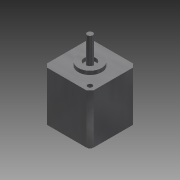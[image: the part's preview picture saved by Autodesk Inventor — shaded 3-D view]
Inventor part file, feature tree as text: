
AUTODESK INVENTOR PART (.ipt)
format: ipt  version: 2013 (Build 170138000, 138)  size: 138,240 bytes
history: native  units: in
note: dims shown in document units (in); Inventor stores cm internally (conversion verified against a paired STEP export)
features: extrude x5, sketch x5
ambient origin geometry x8: Origin, YZ Plane, XZ Plane, XY Plane, X Axis, Y Axis, Z Axis, Center Point
bodies: Solid1 (feature_tree)
feature tree (10):
  extrude  "Extrusion1"  Depth=1.0in
  extrude  "Extrusion2"  Depth=0.5in
  extrude  "Extrusion3"  Depth=0.0787in
  extrude  "Extrusion4"  Depth=0.0787in
  extrude  "Extrusion5"  Depth=0.0787in
  sketch  "Sketch1"  dims[d0=1.0in d2=1.0in]
  sketch  "Sketch2"  dims[d3=0.5in d4=0.5in]
  sketch  "Sketch3"  dims[d5=0.0787in d6=0.0787in]
  sketch  "Sketch4"  dims[d7=0.0787in d8=0.0787in]
  sketch  "Sketch5"  dims[d9=0.0787in d10=0.0787in d11=0.0787in d12=0.0787in d13=0.125in d14=0.125in d15=0.125in d16=0.125in d17=0.1in d18=0.1in d19=1.0625in d20=0.0in d21=0.5in d23=0.25in d24=0.0787in d25=0.0in d26=0.1181in d28=0.5906in d29=0.0in d30=0.1181in d32=0.4375in d33=0.0in d34=0.375in d35=0.375in d36=0.0625in d37=0.0625in d38=0.0938in d39=0.0in]
